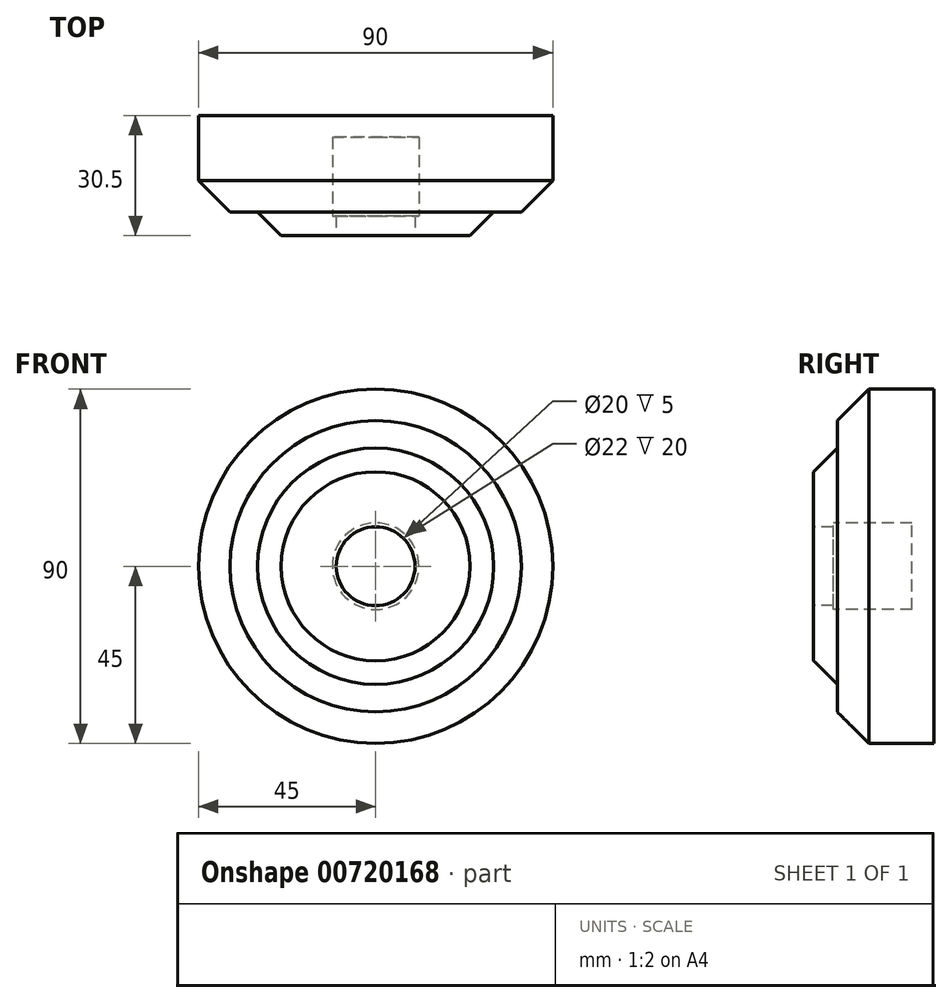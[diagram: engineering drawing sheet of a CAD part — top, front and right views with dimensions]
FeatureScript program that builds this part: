
annotation { "Feature Type Name" : "Feature", "Feature Type Description" : "" }
export const myFeature = defineFeature(function(context is Context, id is Id, definition is map)
    precondition{}
    {
        {
            var Q0;
            Q0=qCreatedBy(makeId("Front.planeOp"),FACE);
            var sketch = newSketch(context, id + "F0", { "sketchPlane" : qUnion([Q0])});
            skCircle(sketch, "E0", {"center": v(0, 0) * mm, "radius": 45 * mm});
            skSolve(sketch);
        }
        {
            var Q0;
            Q0=qSketchRegion(id+"F0",true);
            extrude(context, id + "F1", {"entities" : qUnion([Q0]), "depth" : 25.5 * mm, "offsetDistance" : 25 * mm});
        }
        {
            var Q0;
            Q0=makeQuery(id+"F1.opExtrude","CAP_FACE",FACE,{"disambiguationData":[OSD([sQuery(id+"F0.wireOp",EDGE,"E0")])],"isStart":true});
            var sketch = newSketch(context, id + "F2", { "sketchPlane" : qUnion([Q0])});
            skCircle(sketch, "E1", {"center": v(0, 0) * mm, "radius": 58 * mm});
            skSolve(sketch);
        }
        {
            var Q0;
            Q0=qSketchRegion(id+"F2",true);
            extrude(context, id + "F3", {"entities" : qUnion([Q0]), "operationType" : NewBodyOperationType.REMOVE, "oppositeDirection" : true, "depth" : 1 * mm, "offsetDistance" : 25 * mm});
        }
        {
            var Q0;
            Q0=makeQuery(id+"F1.opExtrude","CAP_EDGE",EDGE,{"disambiguationData":[OSD([sQuery(id+"F0.wireOp",EDGE,"E0")])],"isStart":false});
            chamfer(context, id + "F4", {"entities" : qUnion([Q0]), "width" : 8 * mm, "tangentPropagation" : true});
        }
        {
            var Q0;
            Q0=makeQuery(id+"F1.opExtrude","CAP_FACE",FACE,{"disambiguationData":[OSD([sQuery(id+"F0.wireOp",EDGE,"E0")])],"isStart":false});
            var sketch = newSketch(context, id + "F5", { "sketchPlane" : qUnion([Q0])});
            skCircle(sketch, "E2", {"center": v(0, 0) * mm, "radius": 30 * mm});
            skSolve(sketch);
        }
        {
            var Q0;
            Q0=makeQuery(id+"F5.imprint","IMPRINT",FACE,{"disambiguationData":[TD([[makeQuery(id+"F5.imprint","IMPRINT",EDGE,{"derivedFrom":sQuery(id+"F5.wireOp",EDGE,"E2")}),1.0]])]});
            extrude(context, id + "F6", {"entities" : qUnion([Q0]), "operationType" : NewBodyOperationType.ADD, "depth" : 6 * mm, "offsetDistance" : 25 * mm});
        }
        {
            var Q0;
            Q0=makeQuery(id+"F6.opExtrude","CAP_EDGE",EDGE,{"disambiguationData":[OSD([sQuery(id+"F5.wireOp",EDGE,"E2")])],"isStart":false});
            chamfer(context, id + "F7", {"entities" : qUnion([Q0]), "width" : 6 * mm, "tangentPropagation" : true});
        }
        {
            var Q0;
            Q0=makeQuery(id+"F6.opExtrude","CAP_FACE",FACE,{"disambiguationData":[OSD([sQuery(id+"F5.wireOp",EDGE,"E2")])],"isStart":false});
            var sketch = newSketch(context, id + "F8", { "sketchPlane" : qUnion([Q0])});
            skPoint(sketch, "E3", {"position": v(0, 0) * mm});
            skSolve(sketch);
        }
        {
            var Q0;
            {var subQ0=sQuery(id+"F5.wireOp",EDGE,"E2");Q0=makeQuery(id+"F8.imprint","IMPRINT",FACE,{"disambiguationData":[TD([[makeQuery(id+"F8.imprint","IMPRINT",EDGE,{"derivedFrom":makeQuery(id+"F7.opChamfer","BLEND_EDGE",EDGE,{"blendedFrom":[makeQuery(id+"F6.opExtrude","CAP_EDGE",EDGE,{"disambiguationData":[OSD([subQ0])],"isStart":false}),makeQuery(id+"F6.opExtrude","CAP_FACE",FACE,{"disambiguationData":[OSD([subQ0])],"isStart":false})],"blendedInto":[makeQuery(id+"F6.opExtrude","CAP_FACE",FACE,{"disambiguationData":[OSD([subQ0])],"isStart":false})]})}),1.0]])]});}
            var sketch = newSketch(context, id + "F9", { "sketchPlane" : qUnion([Q0])});
            skCircle(sketch, "E4", {"center": v(0, 0) * mm, "radius": 11 * mm});
            skSolve(sketch);
        }
        {
            var Q0;
            Q0=makeQuery(id+"F9.imprint","IMPRINT",FACE,{"disambiguationData":[TD([[makeQuery(id+"F9.imprint","IMPRINT",EDGE,{"derivedFrom":sQuery(id+"F9.wireOp",EDGE,"E4")}),1.0]])]});
            extrude(context, id + "F10", {"entities" : qUnion([Q0]), "operationType" : NewBodyOperationType.REMOVE, "oppositeDirection" : true, "depth" : 25 * mm, "offsetDistance" : 25 * mm});
        }
        {
            var Q0;
            {var subQ0=sQuery(id+"F5.wireOp",EDGE,"E2");Q0=makeQuery(id+"F8.imprint","IMPRINT",FACE,{"disambiguationData":[TD([[makeQuery(id+"F8.imprint","IMPRINT",EDGE,{"derivedFrom":makeQuery(id+"F7.opChamfer","BLEND_EDGE",EDGE,{"blendedFrom":[makeQuery(id+"F6.opExtrude","CAP_EDGE",EDGE,{"disambiguationData":[OSD([subQ0])],"isStart":false}),makeQuery(id+"F6.opExtrude","CAP_FACE",FACE,{"disambiguationData":[OSD([subQ0])],"isStart":false})],"blendedInto":[makeQuery(id+"F6.opExtrude","CAP_FACE",FACE,{"disambiguationData":[OSD([subQ0])],"isStart":false})]})}),1.0]])]});}
            var sketch = newSketch(context, id + "F11", { "sketchPlane" : qUnion([Q0])});
            skCircle(sketch, "E5", {"center": v(0, 0) * mm, "radius": 11 * mm});
            skCircle(sketch, "E6", {"center": v(0, 0) * mm, "radius": 10 * mm});
            skSolve(sketch);
        }
        {
            var Q0;
            Q0 = qSketchRegion(id + "F11", true);
            extrude(context, id + "F12", {"entities" : qUnion([Q0]), "operationType" : NewBodyOperationType.ADD, "oppositeDirection" : true, "depth" : 5 * mm, "offsetDistance" : 25 * mm});
        }
    });
